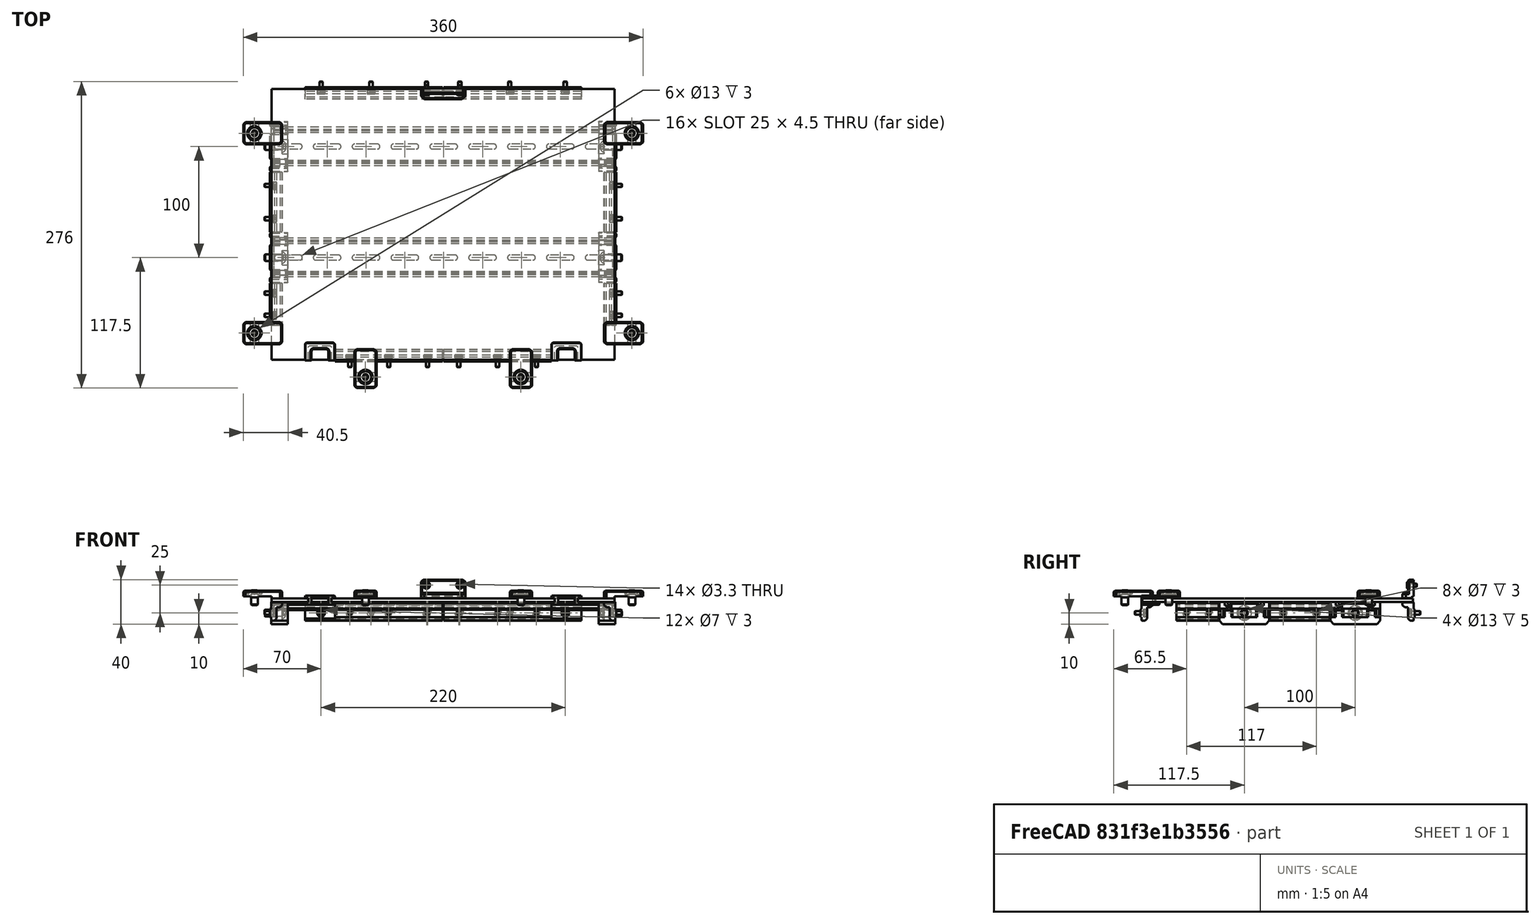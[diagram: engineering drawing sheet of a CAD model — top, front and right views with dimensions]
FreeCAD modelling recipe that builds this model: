
FCSTD DOCUMENT  (FreeCAD 0.19R24291 (Git))
Label: back-panel-assembly
License: Other
LicenseURL: GPL3
objects: Part::FeaturePython×32, Part::Feature×23, Part::Box×1, App::Part×1
note: 56 computed .brp shape members not serialized (recipe doc carries the construction recipe); baked Part::Feature solids carry a one-line shape summary decoded from their .brp

FEATURE [Part::Box] Box  label="panel-309x244mm"
  AttacherType = Attacher::AttachEngine3D
  Height = 3
  Length = 309
  Placement = pos=(-154.5,-134,-5) rot=(0,0,1;0rad)
  Width = 244
FEATURE [Part::Feature] Common001003002002001  label="din-309mm"
  Placement = pos=(0,-4,15) rot=(1,0,0;3.14159rad)
  shape: bbox 305 x 35 x 7.5 mm, 68 faces (baked)
FEATURE [Part::Feature] Common001003002002002  label="din-309mm001"
  Placement = pos=(0,96,15) rot=(1,0,0;3.14159rad)
  shape: bbox 305 x 35 x 7.5 mm, 68 faces (baked)
FEATURE [Part::FeaturePython] Screw  label="M6x16-Screw"  # Fasteners workbench fastener (typed FeaturePython)
  Placement = pos=(-145,58,-15) rot=(0,1,0;1.5708rad)
  diameter = 4
  invert = false
  length = 13
  lengthCustom = 16
  matchOuter = true
  offset = 0
  thread = false
  type = 39
FEATURE [Part::FeaturePython] Screw001  label="M6x16-Screw007"  # Fasteners workbench fastener (typed FeaturePython)
  Placement = pos=(-145,-42,-15) rot=(0,1,0;1.5708rad)
  diameter = 4
  invert = false
  length = 13
  lengthCustom = 16
  matchOuter = true
  offset = 0
  thread = false
  type = 39
FEATURE [Part::FeaturePython] Screw002  label="M6x16-Screw008"  # Fasteners workbench fastener (typed FeaturePython)
  Placement = pos=(145,-42,-15) rot=(0,-1,0;1.5708rad)
  diameter = 4
  invert = false
  length = 13
  lengthCustom = 16
  matchOuter = true
  offset = 0
  thread = false
  type = 39
FEATURE [Part::FeaturePython] Screw003  label="M6x16-Screw006"  # Fasteners workbench fastener (typed FeaturePython)
  Placement = pos=(145,58,-15) rot=(0,-1,0;1.5708rad)
  diameter = 4
  invert = false
  length = 13
  lengthCustom = 16
  matchOuter = true
  offset = 0
  thread = false
  type = 39
FEATURE [Part::Feature] Cut008004003004014002002005003004003002003001003001001  label="back-btm-pannel-inner-clip001"
  Placement = pos=(-155,60,5) rot=(-1,0,0;1.5708rad)
  shape: bbox 35 x 20 x 7 mm, 27 faces (baked)
FEATURE [Part::Feature] Cut008004003004014002002005003004003002003001003001002  label="back-btm-pannel-inner-clip002"
  Placement = pos=(-155,-120,5) rot=(-1,0,0;1.5708rad)
  shape: bbox 35 x 20 x 7 mm, 27 faces (baked)
FEATURE [Part::Feature] Cut008004003004014002002005003004003002003001003001003  label="back-btm-pannel-inner-clip003"
  Placement = pos=(-60,-134.5,5) rot=(0.57735,0.57735,-0.57735;4.18879rad)
  shape: bbox 20 x 35 x 7 mm, 27 faces (baked)
FEATURE [Part::Feature] Cut008004003004014002002005003004003002003001003001004  label="back-btm-pannel-inner-clip004"
  Placement = pos=(80,-134.5,5) rot=(0.57735,0.57735,-0.57735;4.18879rad)
  shape: bbox 20 x 35 x 7 mm, 27 faces (baked)
FEATURE [Part::Feature] Cut008004003004014002002005003004003002003001003001005  label="back-btm-pannel-inner-clip005"
  Placement = pos=(155,-100,5) rot=(0,0.707107,-0.707107;3.14159rad)
  shape: bbox 35 x 20 x 7 mm, 27 faces (baked)
FEATURE [Part::Feature] Cut008004003004014002002005003004003002003001003001006  label="back-btm-pannel-inner-clip006"
  Placement = pos=(155,80,5) rot=(0,0.707107,-0.707107;3.14159rad)
  shape: bbox 35 x 20 x 7 mm, 27 faces (baked)
FEATURE [Part::FeaturePython] Screw028  label="M6x10-Screw"  # Fasteners workbench fastener (typed FeaturePython)
  Placement = pos=(-170,70,2) rot=(0,0,1;0rad)
  baseObject = -> Cut008004003004014002002005003004003002003001003001001 [Edge24]
  diameter = 4
  invert = true
  length = 0
  lengthCustom = 10
  matchOuter = true
  offset = 0
  thread = false
  type = 39
FEATURE [Part::FeaturePython] Screw029  label="M6x10-Screw006"  # Fasteners workbench fastener (typed FeaturePython)
  Placement = pos=(-170,-110,2) rot=(0,0,1;0rad)
  baseObject = -> Cut008004003004014002002005003004003002003001003001002 [Edge24]
  diameter = 4
  invert = true
  length = 0
  lengthCustom = 10
  matchOuter = true
  offset = 0
  thread = false
  type = 39
FEATURE [Part::FeaturePython] Screw030  label="M6x10-Screw007"  # Fasteners workbench fastener (typed FeaturePython)
  Placement = pos=(-70,-149.5,2) rot=(0,0,1;0rad)
  baseObject = -> Cut008004003004014002002005003004003002003001003001003 [Edge24]
  diameter = 4
  invert = true
  length = 0
  lengthCustom = 10
  matchOuter = true
  offset = 0
  thread = false
  type = 39
FEATURE [Part::FeaturePython] Screw031  label="M6x10-Screw008"  # Fasteners workbench fastener (typed FeaturePython)
  Placement = pos=(70,-149.5,2) rot=(0,0,1;0rad)
  baseObject = -> Cut008004003004014002002005003004003002003001003001004 [Edge24]
  diameter = 4
  invert = true
  length = 0
  lengthCustom = 10
  matchOuter = true
  offset = 0
  thread = false
  type = 39
FEATURE [Part::FeaturePython] Screw032  label="M6x10-Screw009"  # Fasteners workbench fastener (typed FeaturePython)
  Placement = pos=(170,70,2) rot=(0,0,1;0rad)
  baseObject = -> Cut008004003004014002002005003004003002003001003001006 [Edge24]
  diameter = 4
  invert = true
  length = 0
  lengthCustom = 10
  matchOuter = true
  offset = 0
  thread = false
  type = 39
FEATURE [Part::FeaturePython] Screw033  label="M6x10-Screw010"  # Fasteners workbench fastener (typed FeaturePython)
  Placement = pos=(170,-110,2) rot=(0,0,1;0rad)
  baseObject = -> Cut008004003004014002002005003004003002003001003001005 [Edge24]
  diameter = 4
  invert = true
  length = 0
  lengthCustom = 10
  matchOuter = true
  offset = 0
  thread = false
  type = 39
FEATURE [Part::Feature] Fusion001001001
  Placement = pos=(-140,58,10) rot=(0,-1,0;1.5708rad)
  shape: bbox 16 x 45 x 20 mm, 55 faces (baked)
FEATURE [Part::Feature] Fusion001001002
  Placement = pos=(-140,-42,10) rot=(0,-1,0;1.5708rad)
  shape: bbox 16 x 45 x 20 mm, 55 faces (baked)
FEATURE [Part::Feature] Fusion001001003
  Placement = pos=(140,-42,10) rot=(0.707107,0,0.707107;3.14159rad)
  shape: bbox 16 x 45 x 20 mm, 55 faces (baked)
FEATURE [Part::Feature] Fusion001001004
  Placement = pos=(140,58,10) rot=(0.707107,0,0.707107;3.14159rad)
  shape: bbox 16 x 45 x 20 mm, 55 faces (baked)
FEATURE [Part::Feature] Cut008004003004014002002005003004003002003001003001002001001
  Placement = pos=(2e-15,110.5,15) rot=(0,0.707107,-0.707107;3.14159rad)
  shape: bbox 40 x 10 x 16.5 mm, 30 faces (baked)
FEATURE [Part::Feature] Cut008004003004014002002005003004003002003001003001002001002001001  label="gasket-54mm002"
  Placement = pos=(-155,8,-15) rot=(0.57735,-0.57735,0.57735;4.18879rad)
  shape: bbox 11 x 54 x 16.5 mm, 23 faces (baked)
FEATURE [Part::Feature] Cut008004003004014002002005003004003002003001003001002001002001002  label="gasket-54mm003"
  Placement = pos=(155,8,-15) rot=(0.57735,0.57735,-0.57735;4.18879rad)
  shape: bbox 11 x 54 x 16.5 mm, 23 faces (baked)
FEATURE [Part::Feature] Cut008004003004014002002005003004003002003001003001002001002002001001  label="gasket-124mm002"
  Placement = pos=(-65,110.5,-15) rot=(0,0.707107,-0.707107;3.14159rad)
  shape: bbox 124 x 11 x 16.5 mm, 26 faces (baked)
FEATURE [Part::Feature] Cut008004003004014002002005003004003002003001003001002001002002001002  label="gasket-124mm003"
  Placement = pos=(60,110.5,-15) rot=(0,0.707107,-0.707107;3.14159rad)
  shape: bbox 124 x 11 x 16.5 mm, 26 faces (baked)
FEATURE [Part::FeaturePython] Screw034  label="M3x8-Screw"  # Fasteners workbench fastener (typed FeaturePython)
  Placement = pos=(-110,108.5,-15) rot=(1,0,0;1.5708rad)
  baseObject = -> Cut008004003004014002002005003004003002003001003001002001002002001001 [Edge49]
  diameter = 4
  invert = false
  length = 2
  lengthCustom = 8
  matchOuter = true
  offset = 0
  thread = false
  type = 33
FEATURE [Part::FeaturePython] Screw035  label="M3x8-Screw001"  # Fasteners workbench fastener (typed FeaturePython)
  Placement = pos=(-65,108.5,-15) rot=(1,0,0;1.5708rad)
  baseObject = -> Cut008004003004014002002005003004003002003001003001002001002002001001 [Edge44]
  diameter = 4
  invert = false
  length = 2
  lengthCustom = 8
  matchOuter = true
  offset = 0
  thread = false
  type = 33
FEATURE [Part::FeaturePython] Screw036  label="M3x8-Screw002"  # Fasteners workbench fastener (typed FeaturePython)
  Placement = pos=(-15,108.5,-15) rot=(1,0,0;1.5708rad)
  baseObject = -> Cut008004003004014002002005003004003002003001003001002001002002001001 [Edge54]
  diameter = 4
  invert = false
  length = 2
  lengthCustom = 8
  matchOuter = true
  offset = 0
  thread = false
  type = 33
FEATURE [Part::FeaturePython] Screw037  label="M3x8-Screw003"  # Fasteners workbench fastener (typed FeaturePython)
  Placement = pos=(15,108.5,-15) rot=(1,0,0;1.5708rad)
  baseObject = -> Cut008004003004014002002005003004003002003001003001002001002002001002 [Edge49]
  diameter = 4
  invert = false
  length = 2
  lengthCustom = 8
  matchOuter = true
  offset = 0
  thread = false
  type = 33
FEATURE [Part::FeaturePython] Screw038  label="M3x8-Screw004"  # Fasteners workbench fastener (typed FeaturePython)
  Placement = pos=(60,108.5,-15) rot=(1,0,0;1.5708rad)
  baseObject = -> Cut008004003004014002002005003004003002003001003001002001002002001002 [Edge44]
  diameter = 4
  invert = false
  length = 2
  lengthCustom = 8
  matchOuter = true
  offset = 0
  thread = false
  type = 33
FEATURE [Part::FeaturePython] Screw039  label="M3x8-Screw005"  # Fasteners workbench fastener (typed FeaturePython)
  Placement = pos=(110,108.5,-15) rot=(1,0,0;1.5708rad)
  baseObject = -> Cut008004003004014002002005003004003002003001003001002001002002001002 [Edge54]
  diameter = 4
  invert = false
  length = 2
  lengthCustom = 8
  matchOuter = true
  offset = 0
  thread = false
  type = 33
FEATURE [Part::FeaturePython] Screw046  label="M3x6-Screw"  # Fasteners workbench fastener (typed FeaturePython)
  Placement = pos=(15,107.5,10) rot=(1,0,0;1.5708rad)
  baseObject = -> Cut008004003004014002002005003004003002003001003001002001001 [Edge37]
  diameter = 4
  invert = false
  length = 1
  lengthCustom = 6
  matchOuter = true
  offset = 0
  thread = false
  type = 33
FEATURE [Part::FeaturePython] Screw047  label="M3x6-Screw001"  # Fasteners workbench fastener (typed FeaturePython)
  Placement = pos=(-15,107.5,10) rot=(1,0,0;1.5708rad)
  baseObject = -> Cut008004003004014002002005003004003002003001003001002001001 [Edge39]
  diameter = 4
  invert = false
  length = 1
  lengthCustom = 6
  matchOuter = true
  offset = 0
  thread = false
  type = 33
FEATURE [Part::Feature] Chamfer002004  label="10x15-hole004"
  Placement = pos=(-103.5,-134.5,-7.5) rot=(0,0.707107,0.707107;3.14159rad)
  shape: bbox 27 x 16 x 8 mm, 50 faces (baked)
FEATURE [Part::Feature] Chamfer002005  label="10x15-hole005"
  Placement = pos=(118.5,-134.5,-7.5) rot=(0,0.707107,0.707107;3.14159rad)
  shape: bbox 27 x 16 x 8 mm, 50 faces (baked)
FEATURE [Part::Feature] Cut008004003004014002002005003004003002003001003001002001002002002001  label="gasket-38mm001"
  Placement = pos=(155,-84,-15) rot=(0.57735,0.57735,-0.57735;4.18879rad)
  shape: bbox 11 x 38 x 16.5 mm, 23 faces (baked)
FEATURE [Part::Feature] Cut008004003004014002002005003004003002003001003001002001002002002002  label="gasket-38mm002"
  Placement = pos=(-155,-84,-15) rot=(0.57735,-0.57735,0.57735;4.18879rad)
  shape: bbox 11 x 38 x 16.5 mm, 23 faces (baked)
FEATURE [Part::Feature] Cut008004003004014002002005003004003002003001003001002001002002003001  label="gasket-97mm001"
  Placement = pos=(49,-134.5,-15) rot=(-1,0,0;1.5708rad)
  shape: bbox 97 x 11 x 16.5 mm, 26 faces (baked)
FEATURE [Part::Feature] Cut008004003004014002002005003004003002003001003001002001002002003002  label="gasket-97mm002"
  Placement = pos=(-49,-134.5,-15) rot=(-1,0,0;1.5708rad)
  shape: bbox 97 x 11 x 16.5 mm, 26 faces (baked)
FEATURE [Part::FeaturePython] Screw048  label="M3x8-Screw006"  # Fasteners workbench fastener (typed FeaturePython)
  Placement = pos=(-84,-132.5,-15) rot=(-1,0,0;1.5708rad)
  baseObject = -> Cut008004003004014002002005003004003002003001003001002001002002003002 [Edge57]
  diameter = 4
  invert = false
  length = 2
  lengthCustom = 8
  matchOuter = true
  offset = 0
  thread = false
  type = 33
FEATURE [Part::FeaturePython] Screw049  label="M3x8-Screw007"  # Fasteners workbench fastener (typed FeaturePython)
  Placement = pos=(-49,-132.5,-15) rot=(-1,0,0;1.5708rad)
  baseObject = -> Cut008004003004014002002005003004003002003001003001002001002002003002 [Edge55]
  diameter = 4
  invert = false
  length = 2
  lengthCustom = 8
  matchOuter = true
  offset = 0
  thread = false
  type = 33
FEATURE [Part::FeaturePython] Screw050  label="M3x8-Screw008"  # Fasteners workbench fastener (typed FeaturePython)
  Placement = pos=(-14,-132.5,-15) rot=(-1,0,0;1.5708rad)
  baseObject = -> Cut008004003004014002002005003004003002003001003001002001002002003002 [Edge53]
  diameter = 4
  invert = false
  length = 2
  lengthCustom = 8
  matchOuter = true
  offset = 0
  thread = false
  type = 33
FEATURE [Part::FeaturePython] Screw051  label="M3x8-Screw009"  # Fasteners workbench fastener (typed FeaturePython)
  Placement = pos=(14,-132.5,-15) rot=(-1,0,0;1.5708rad)
  baseObject = -> Cut008004003004014002002005003004003002003001003001002001002002003001 [Edge57]
  diameter = 4
  invert = false
  length = 2
  lengthCustom = 8
  matchOuter = true
  offset = 0
  thread = false
  type = 33
FEATURE [Part::FeaturePython] Screw052  label="M3x8-Screw010"  # Fasteners workbench fastener (typed FeaturePython)
  Placement = pos=(49,-132.5,-15) rot=(-1,0,0;1.5708rad)
  baseObject = -> Cut008004003004014002002005003004003002003001003001002001002002003001 [Edge55]
  diameter = 4
  invert = false
  length = 2
  lengthCustom = 8
  matchOuter = true
  offset = 0
  thread = false
  type = 33
FEATURE [Part::FeaturePython] Screw053  label="M3x8-Screw011"  # Fasteners workbench fastener (typed FeaturePython)
  Placement = pos=(84,-132.5,-15) rot=(-1,0,0;1.5708rad)
  baseObject = -> Cut008004003004014002002005003004003002003001003001002001002002003001 [Edge53]
  diameter = 4
  invert = false
  length = 2
  lengthCustom = 8
  matchOuter = true
  offset = 0
  thread = false
  type = 33
FEATURE [Part::FeaturePython] Screw054  label="M3x8-Screw012"  # Fasteners workbench fastener (typed FeaturePython)
  Placement = pos=(-153,23,-15) rot=(0,1,0;1.5708rad)
  baseObject = -> Cut008004003004014002002005003004003002003001003001002001002001001 [Edge52]
  diameter = 4
  invert = false
  length = 2
  lengthCustom = 8
  matchOuter = true
  offset = 0
  thread = false
  type = 33
FEATURE [Part::FeaturePython] Screw055  label="M3x8-Screw013"  # Fasteners workbench fastener (typed FeaturePython)
  Placement = pos=(-153,-7,-15) rot=(0,1,0;1.5708rad)
  baseObject = -> Cut008004003004014002002005003004003002003001003001002001002001001 [Edge45]
  diameter = 4
  invert = false
  length = 2
  lengthCustom = 8
  matchOuter = true
  offset = 0
  thread = false
  type = 33
FEATURE [Part::FeaturePython] Screw056  label="M3x8-Screw014"  # Fasteners workbench fastener (typed FeaturePython)
  Placement = pos=(-153,-74,-15) rot=(0,1,0;1.5708rad)
  baseObject = -> Cut008004003004014002002005003004003002003001003001002001002002002002 [Edge53]
  diameter = 4
  invert = false
  length = 2
  lengthCustom = 8
  matchOuter = true
  offset = 0
  thread = false
  type = 33
FEATURE [Part::FeaturePython] Screw057  label="M3x8-Screw015"  # Fasteners workbench fastener (typed FeaturePython)
  Placement = pos=(-153,-94,-15) rot=(0,1,0;1.5708rad)
  baseObject = -> Cut008004003004014002002005003004003002003001003001002001002002002002 [Edge51]
  diameter = 4
  invert = false
  length = 2
  lengthCustom = 8
  matchOuter = true
  offset = 0
  thread = false
  type = 33
FEATURE [Part::FeaturePython] Screw058  label="M3x8-Screw016"  # Fasteners workbench fastener (typed FeaturePython)
  Placement = pos=(153,23,-15) rot=(0,-1,0;1.5708rad)
  baseObject = -> Cut008004003004014002002005003004003002003001003001002001002001002 [Edge45]
  diameter = 4
  invert = false
  length = 2
  lengthCustom = 8
  matchOuter = true
  offset = 0
  thread = false
  type = 33
FEATURE [Part::FeaturePython] Screw059  label="M3x8-Screw017"  # Fasteners workbench fastener (typed FeaturePython)
  Placement = pos=(153,-7,-15) rot=(0,-1,0;1.5708rad)
  baseObject = -> Cut008004003004014002002005003004003002003001003001002001002001002 [Edge52]
  diameter = 4
  invert = false
  length = 2
  lengthCustom = 8
  matchOuter = true
  offset = 0
  thread = false
  type = 33
FEATURE [Part::FeaturePython] Screw060  label="M3x8-Screw018"  # Fasteners workbench fastener (typed FeaturePython)
  Placement = pos=(153,-74,-15) rot=(0,-1,0;1.5708rad)
  baseObject = -> Cut008004003004014002002005003004003002003001003001002001002002002001 [Edge51]
  diameter = 4
  invert = false
  length = 2
  lengthCustom = 8
  matchOuter = true
  offset = 0
  thread = false
  type = 33
FEATURE [Part::FeaturePython] Screw061  label="M3x8-Screw019"  # Fasteners workbench fastener (typed FeaturePython)
  Placement = pos=(153,-94,-15) rot=(0,-1,0;1.5708rad)
  baseObject = -> Cut008004003004014002002005003004003002003001003001002001002002002001 [Edge53]
  diameter = 4
  invert = false
  length = 2
  lengthCustom = 8
  matchOuter = true
  offset = 0
  thread = false
  type = 33
FEATURE [App::Part] Part  label="back-bottom-panel"
  Group = -> [Common001003002002001,Box,Common001003002002002,Screw,Screw001,Screw002,Screw003,Screw028,Cut008004003004014002002005003004003002003001003001001,Screw029,Cut008004003004014002002005003004003002003001003001002,Screw030,Cut008004003004014002002005003004003002003001003001003,Screw031,Cut008004003004014002002005003004003002003001003001004,Screw033,+40 more]
  Origin = -> Origin
